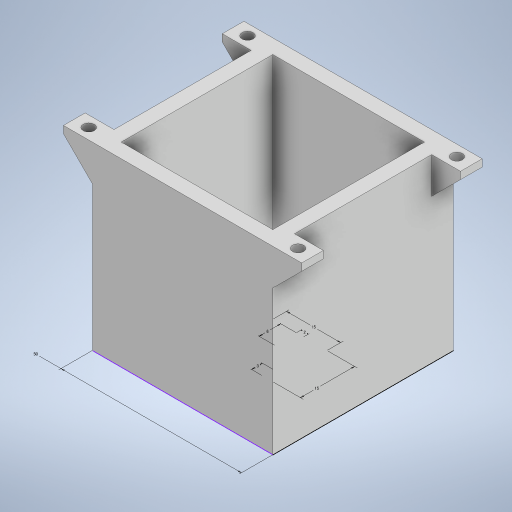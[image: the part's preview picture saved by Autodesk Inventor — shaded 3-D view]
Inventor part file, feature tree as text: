
AUTODESK INVENTOR PART (.ipt)
format: ipt  version: 2024 (Build 280153000, 153)  size: 555,008 bytes
history: native  units: mm
features: sketch x6, extrude x4, mirror x2, hole x2, projected_geometry x2, other x1, chamfer x1
ambient origin geometry x8: Origin, YZ Plane, XZ Plane, XY Plane, X Axis, Y Axis, Z Axis, Center Point
bodies: Body1 (feature_tree)
feature tree (18):
  other  "ソリッド1"
  extrude  "押し出し1"  Depth=50.0mm
  extrude  "押し出し2"  Depth=15.0mm
  extrude  "押し出し3"  Depth=15.0mm
  extrude  "押し出し4"  Depth=3.0mm
  mirror  "ミラー1"
  mirror  "ミラー2"
  chamfer  "面取り2"  Distance=2.0mm
  hole  "穴1"  [1 undecoded]
  hole  "穴2"  [1 undecoded]
  sketch  "スケッチ1"
  sketch  "スケッチ2"
  projected_geometry  "投影ループ1"
  sketch  "スケッチ3"
  sketch  "スケッチ4"
  sketch  "スケッチ5"
  sketch  "スケッチ6"
  projected_geometry  "投影ループ2"
note: 2 required parameter values undecoded (feature->parameter linkage not recoverable at this tier; creation-order binding heuristic only, values carry confidence <= 0.55)
